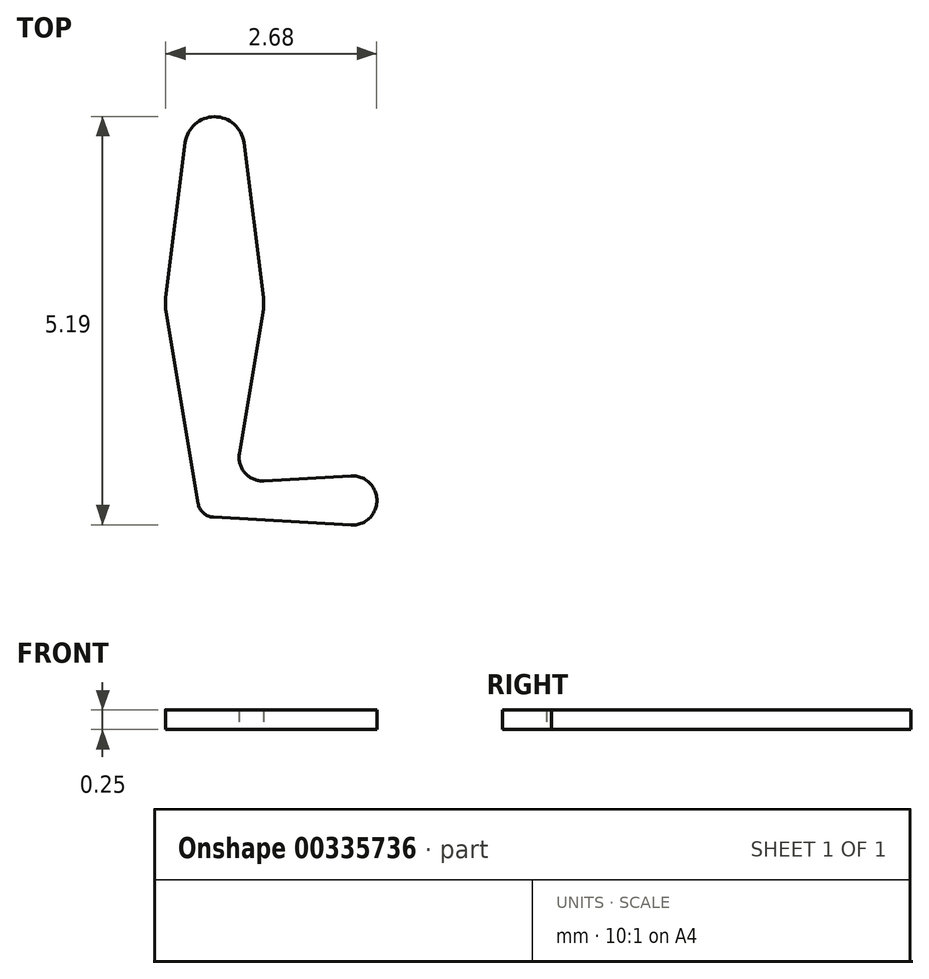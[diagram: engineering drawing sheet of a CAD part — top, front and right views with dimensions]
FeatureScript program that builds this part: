
annotation { "Feature Type Name" : "Feature", "Feature Type Description" : "" }
export const myFeature = defineFeature(function(context is Context, id is Id, definition is map)
    precondition{}
    {
        {
            var Q0;
            Q0=qCreatedBy(makeId("Top.planeOp"),FACE);
            var sketch = newSketch(context, id + "F0", { "sketchPlane" : qUnion([Q0])});
            skLineSegment(sketch, "E0", {"start": v(0, 0) * mm, "end": v(0, 4.5) * mm, "construction": true});
            skCircle(sketch, "E1", {"center": v(0, 0) * mm, "radius": 0.21 * mm});
            skCircle(sketch, "E2", {"center": v(0, 4.5) * mm, "radius": 0.38 * mm});
            skCircle(sketch, "E3", {"center": v(0, 2.5) * mm, "radius": 0.62 * mm});
            skLineSegment(sketch, "E4", {"start": v(0, 0) * mm, "end": v(1.75, 0) * mm, "construction": true});
            skCircle(sketch, "E5", {"center": v(1.75, 0) * mm, "radius": 0.31 * mm});
            skLineSegment(sketch, "E6", {"start": v(-0.37, 4.55) * mm, "end": v(-0.62, 2.58) * mm});
            skLineSegment(sketch, "E7", {"start": v(-0.62, 2.4) * mm, "end": v(-0.2, -0.04) * mm});
            skLineSegment(sketch, "E8", {"start": v(0.32, 0.6) * mm, "end": v(0.62, 2.4) * mm});
            skLineSegment(sketch, "E9", {"start": v(0.62, 2.58) * mm, "end": v(0.37, 4.55) * mm});
            skLineSegment(sketch, "E10", {"start": v(0.63, 0.25) * mm, "end": v(1.73, 0.31) * mm});
            skLineSegment(sketch, "E11", {"start": v(-0.01, -0.21) * mm, "end": v(1.73, -0.31) * mm});
            skPoint(sketch, "E12.newPointA", {"position": v(0.2, -0.04) * mm});
            skArc(sketch, "E12.filletArc", {"start": v(0.32, 0.6) * mm, "mid": v(0.39, 0.35) * mm, "end": v(0.63, 0.25) * mm});
            skSolve(sketch);
        }
        {
            var Q0;
            {var subQ0=sQuery(id+"F0.wireOp",EDGE,"E2");var subQ1=makeQuery(id+"F0.imprint","INTERSECT",VERTEX,{"derivedFrom":[subQ0,sQuery(id+"F0.wireOp",EDGE,"E6")]});Q0=makeQuery(id+"F0.imprint","IMPRINT",FACE,{"disambiguationData":[TD([[makeQuery(id+"F0.imprint","IMPRINT",EDGE,{"disambiguationData":[TD([[subQ1,1.0]])],"derivedFrom":subQ0}),1.0]])]});}
            var Q1;
            {var subQ0=sQuery(id+"F0.wireOp",EDGE,"E6");Q1=makeQuery(id+"F0.imprint","IMPRINT",FACE,{"disambiguationData":[TD([[makeQuery(id+"F0.imprint","IMPRINT",EDGE,{"derivedFrom":subQ0}),1.0]])]});}
            var Q2;
            {var subQ0=sQuery(id+"F0.wireOp",EDGE,"E3");var subQ1=makeQuery(id+"F0.imprint","INTERSECT",VERTEX,{"derivedFrom":[subQ0,sQuery(id+"F0.wireOp",EDGE,"E6")]});Q2=makeQuery(id+"F0.imprint","IMPRINT",FACE,{"disambiguationData":[TD([[makeQuery(id+"F0.imprint","IMPRINT",EDGE,{"disambiguationData":[TD([[subQ1,1.0]])],"derivedFrom":subQ0}),1.0]])]});}
            var Q3;
            {var subQ3=sQuery(id+"F0.wireOp",EDGE,"E7");Q3=makeQuery(id+"F0.imprint","IMPRINT",FACE,{"disambiguationData":[TD([[makeQuery(id+"F0.imprint","IMPRINT",EDGE,{"derivedFrom":subQ3}),1.0]])]});}
            var Q4;
            {var subQ0=sQuery(id+"F0.wireOp",EDGE,"E1");var subQ1=makeQuery(id+"F0.imprint","INTERSECT",VERTEX,{"derivedFrom":[subQ0,sQuery(id+"F0.wireOp",EDGE,"E7")]});Q4=makeQuery(id+"F0.imprint","IMPRINT",FACE,{"disambiguationData":[TD([[makeQuery(id+"F0.imprint","IMPRINT",EDGE,{"disambiguationData":[TD([[subQ1,-1.0]])],"derivedFrom":subQ0}),1.0]])]});}
            var Q5;
            {var subQ0=sQuery(id+"F0.wireOp",EDGE,"E5");var subQ1=makeQuery(id+"F0.imprint","INTERSECT",VERTEX,{"derivedFrom":[subQ0,sQuery(id+"F0.wireOp",EDGE,"E10")]});Q5=makeQuery(id+"F0.imprint","IMPRINT",FACE,{"disambiguationData":[TD([[makeQuery(id+"F0.imprint","IMPRINT",EDGE,{"disambiguationData":[TD([[subQ1,-1.0]])],"derivedFrom":subQ0}),1.0]])]});}
            extrude(context, id + "F1", {"entities" : qUnion([Q0, Q1, Q2, Q3, Q4, Q5]), "depth" : 0.25 * mm});
        }
    });
